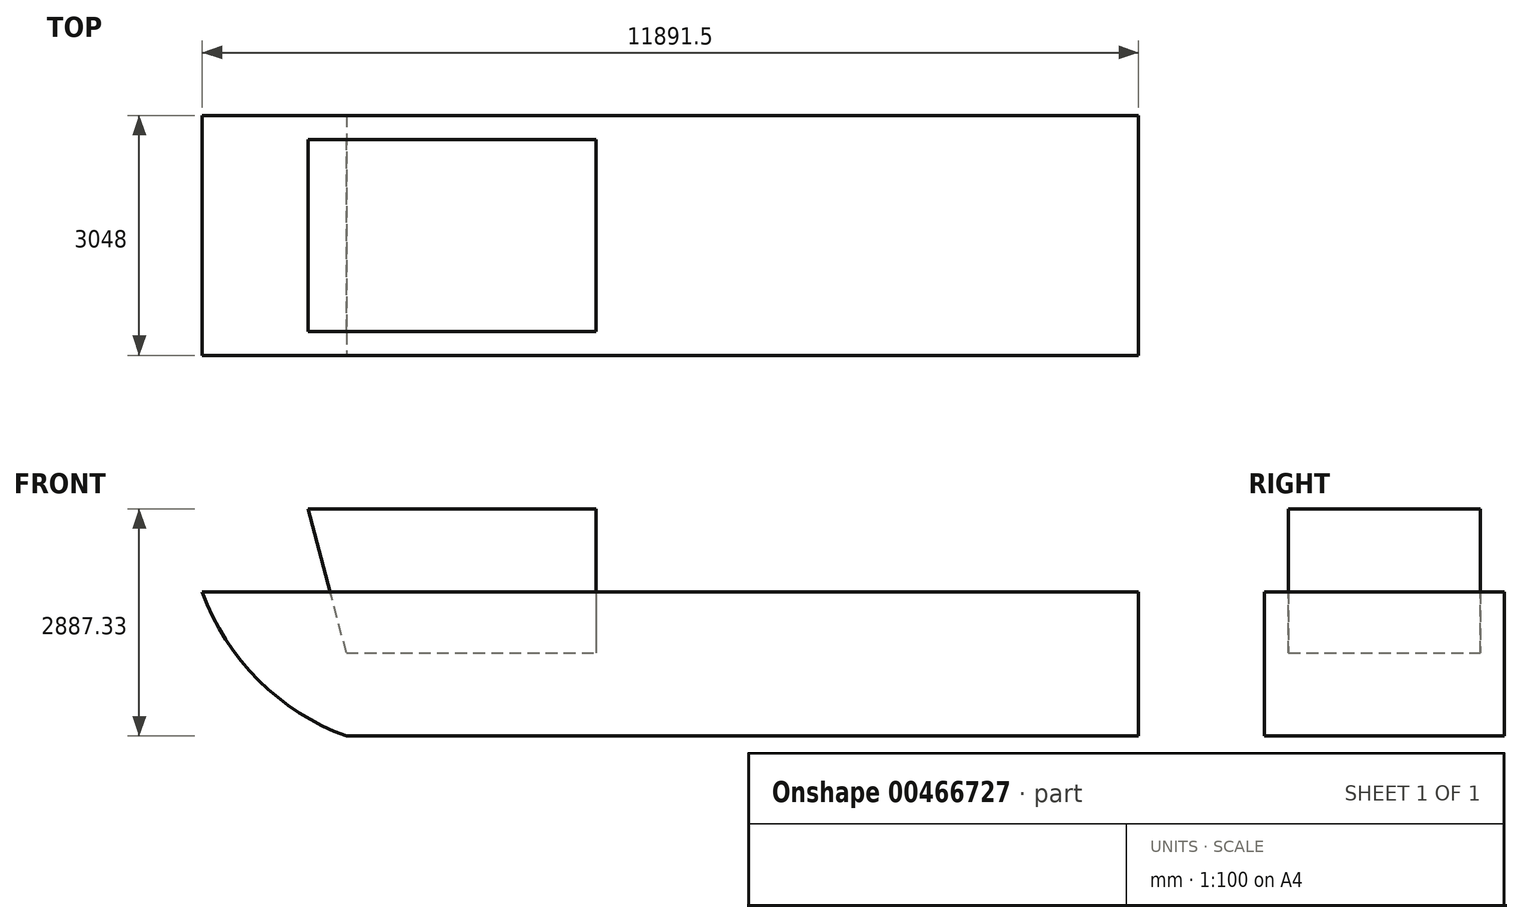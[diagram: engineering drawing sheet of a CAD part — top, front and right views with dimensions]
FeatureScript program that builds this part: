
annotation { "Feature Type Name" : "Feature", "Feature Type Description" : "" }
export const myFeature = defineFeature(function(context is Context, id is Id, definition is map)
    precondition{}
    {
        {
            var Q0;
            Q0=qCreatedBy(makeId("Front.planeOp"),FACE);
            var sketch = newSketch(context, id + "F0", { "sketchPlane" : qUnion([Q0])});
            skLineSegment(sketch, "E0.bottom", {"start": v(-5870.75, 1175.92) * mm, "end": v(6020.74, 1175.92) * mm});
            skLineSegment(sketch, "E0.top", {"start": v(-4037.66, -652.88) * mm, "end": v(6020.74, -652.88) * mm});
            skLineSegment(sketch, "E0.right", {"start": v(6020.74, 1175.92) * mm, "end": v(6020.74, -652.88) * mm});
            skArc(sketch, "E1", {"start": v(-5870.75, 1175.92) * mm, "mid": v(-5158.06, 57.19) * mm, "end": v(-4037.66, -652.88) * mm});
            skSolve(sketch);
        }
        {
            var Q0;
            {var subQ0=sQuery(id+"F0.wireOp",EDGE,"E0.right");Q0=makeQuery(id+"F0.imprint","IMPRINT",FACE,{"disambiguationData":[TD([[makeQuery(id+"F0.imprint","IMPRINT",EDGE,{"derivedFrom":subQ0}),-1.0]])]});}
            extrude(context, id + "F1", {"entities" : qUnion([Q0]), "endBound" : BoundingType.SYMMETRIC, "oppositeDirection" : true, "depth" : 3048 * mm});
        }
        {
            var Q0;
            Q0=qCreatedBy(makeId("Front.planeOp"),FACE);
            var sketch = newSketch(context, id + "F2", { "sketchPlane" : qUnion([Q0])});
            skLineSegment(sketch, "E2.bottom", {"start": v(-6501.05, 405.65) * mm, "end": v(5521.34, 405.65) * mm});
            skLineSegment(sketch, "E2.top", {"start": v(-4537.06, -1423.15) * mm, "end": v(5521.34, -1423.15) * mm});
            skLineSegment(sketch, "E2.right", {"start": v(5521.34, 405.65) * mm, "end": v(5521.34, -1423.15) * mm});
            skArc(sketch, "E3", {"start": v(-6501.05, 405.65) * mm, "mid": v(-5731.15, -736.53) * mm, "end": v(-4537.06, -1423.15) * mm});
            skLineSegment(sketch, "E4", {"start": v(-4039.2, 405.65) * mm, "end": v(-4529.22, 2234.45) * mm});
            skLineSegment(sketch, "E5", {"start": v(-4529.22, 2234.45) * mm, "end": v(-871.62, 2234.45) * mm});
            skLineSegment(sketch, "E6", {"start": v(-871.62, 2234.45) * mm, "end": v(-871.62, 405.65) * mm});
            skSolve(sketch);
        }
        {
            var Q0;
            {var subQ0=sQuery(id+"F2.wireOp",EDGE,"E4");Q0=makeQuery(id+"F2.imprint","IMPRINT",FACE,{"disambiguationData":[TD([[makeQuery(id+"F2.imprint","IMPRINT",EDGE,{"derivedFrom":subQ0}),-1.0]])]});}
            extrude(context, id + "F3", {"entities" : qUnion([Q0]), "endBound" : BoundingType.SYMMETRIC, "depth" : 2438.4 * mm});
        }
    });
